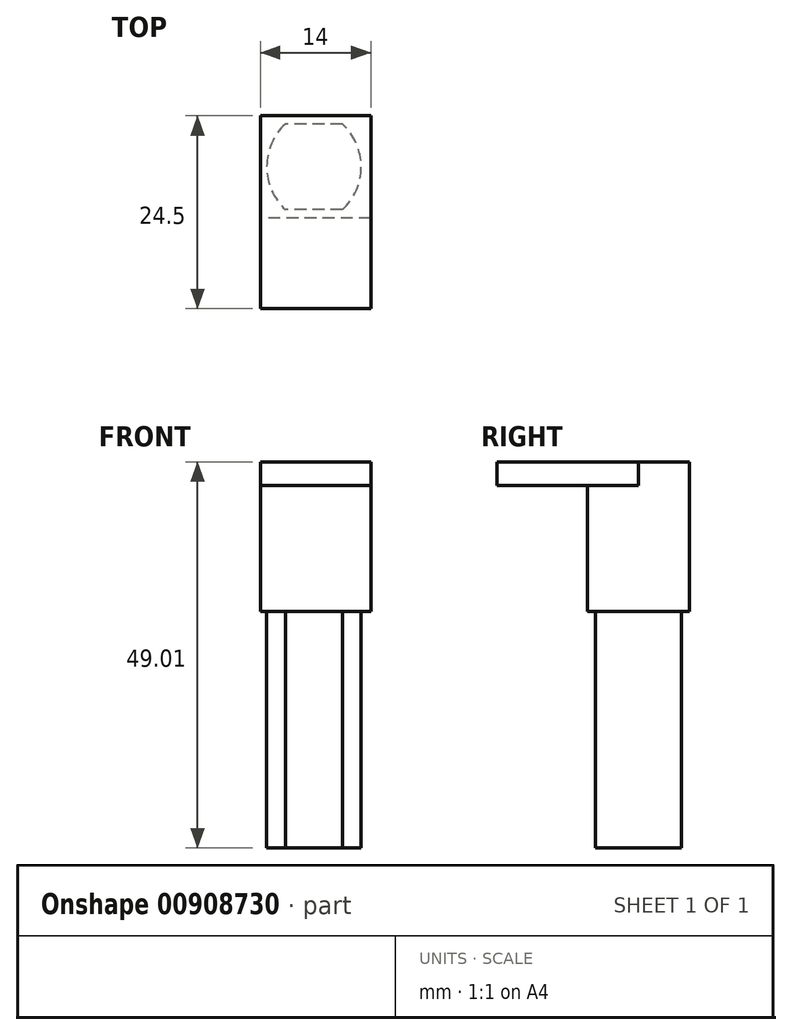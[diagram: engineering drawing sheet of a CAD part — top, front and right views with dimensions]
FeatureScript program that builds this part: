
annotation { "Feature Type Name" : "Feature", "Feature Type Description" : "" }
export const myFeature = defineFeature(function(context is Context, id is Id, definition is map)
    precondition{}
    {
        {
            var Q0;
            Q0=qCreatedBy(makeId("Top.planeOp"),FACE);
            var sketch = newSketch(context, id + "F0", { "sketchPlane" : qUnion([Q0])});
            skLineSegment(sketch, "E0.bottom", {"start": v(3.63, 5.45) * mm, "end": v(-3.62, 5.45) * mm});
            skLineSegment(sketch, "E0.top", {"start": v(3.62, -5.45) * mm, "end": v(-3.63, -5.45) * mm});
            skLineSegment(sketch, "E0.left", {"start": v(3.63, 5.45) * mm, "end": v(3.62, -5.45) * mm});
            skLineSegment(sketch, "E0.right", {"start": v(-3.62, 5.45) * mm, "end": v(-3.63, -5.45) * mm});
            skPoint(sketch, "E0.middle", {"position": v(0, 0) * mm});
            skLineSegment(sketch, "E1", {"start": v(0, 0) * mm, "end": v(-6, 0) * mm});
            skLineSegment(sketch, "E2.MirrorCS", {"start": v(0, 0) * mm, "end": v(6, 0) * mm});
            skArc(sketch, "E3", {"start": v(-3.63, 5.45) * mm, "mid": v(-6, 0) * mm, "end": v(-3.63, -5.45) * mm});
            skArc(sketch, "E4", {"start": v(3.63, -5.45) * mm, "mid": v(6, 0) * mm, "end": v(3.63, 5.45) * mm});
            skSolve(sketch);
        }
        {
            var Q0;
            Q0 = qSketchRegion(id + "F0", true);
            var Q1;
            Q1 = qSketchRegion(id + "F2", true);
            extrude(context, id + "F1", {"entities" : qUnion([Q0, Q1]), "depth" : -30 * mm, "offsetDistance" : 25 * mm});
        }
        {
            var Q0;
            Q0=qCreatedBy(makeId("Top.planeOp"),FACE);
            var sketch = newSketch(context, id + "F2", { "sketchPlane" : qUnion([Q0])});
            skLineSegment(sketch, "E5.bottom", {"start": v(7.22, 6.5) * mm, "end": v(-6.78, 6.5) * mm});
            skLineSegment(sketch, "E5.top", {"start": v(7.22, -6.5) * mm, "end": v(-6.78, -6.5) * mm});
            skLineSegment(sketch, "E5.left", {"start": v(7.22, 6.5) * mm, "end": v(7.22, -6.5) * mm});
            skLineSegment(sketch, "E5.right", {"start": v(-6.78, 6.5) * mm, "end": v(-6.78, -6.5) * mm});
            skPoint(sketch, "E5.middle", {"position": v(0.22, 0) * mm});
            skSolve(sketch);
        }
        {
            var Q0;
            Q0 = qSketchRegion(id + "F2", true);
            extrude(context, id + "F3", {"entities" : qUnion([Q0]), "operationType" : NewBodyOperationType.ADD, "depth" : 19 * mm, "offsetDistance" : 25 * mm});
        }
        {
            var Q0;
            Q0=qCreatedBy(makeId("Front.planeOp"),FACE);
            var sketch = newSketch(context, id + "F4", { "sketchPlane" : qUnion([Q0])});
            skLineSegment(sketch, "E6.bottom", {"start": v(-6.78, 19) * mm, "end": v(7.22, 19) * mm});
            skLineSegment(sketch, "E6.top", {"start": v(-6.78, 16) * mm, "end": v(7.22, 16) * mm});
            skLineSegment(sketch, "E6.left", {"start": v(-6.78, 19) * mm, "end": v(-6.78, 16) * mm});
            skLineSegment(sketch, "E6.right", {"start": v(7.22, 19) * mm, "end": v(7.22, 16) * mm});
            skSolve(sketch);
        }
        {
            var Q0;
            Q0=makeQuery(id+"F4.imprint","IMPRINT",FACE,{"disambiguationData":[TD([[makeQuery(id+"F4.imprint","IMPRINT",EDGE,{"derivedFrom":sQuery(id+"F4.wireOp",EDGE,"E6.bottom")}),-1.0]])]});
            extrude(context, id + "F5", {"entities" : qUnion([Q0]), "operationType" : NewBodyOperationType.ADD, "depth" : 18 * mm, "offsetDistance" : 25 * mm});
        }
    });
